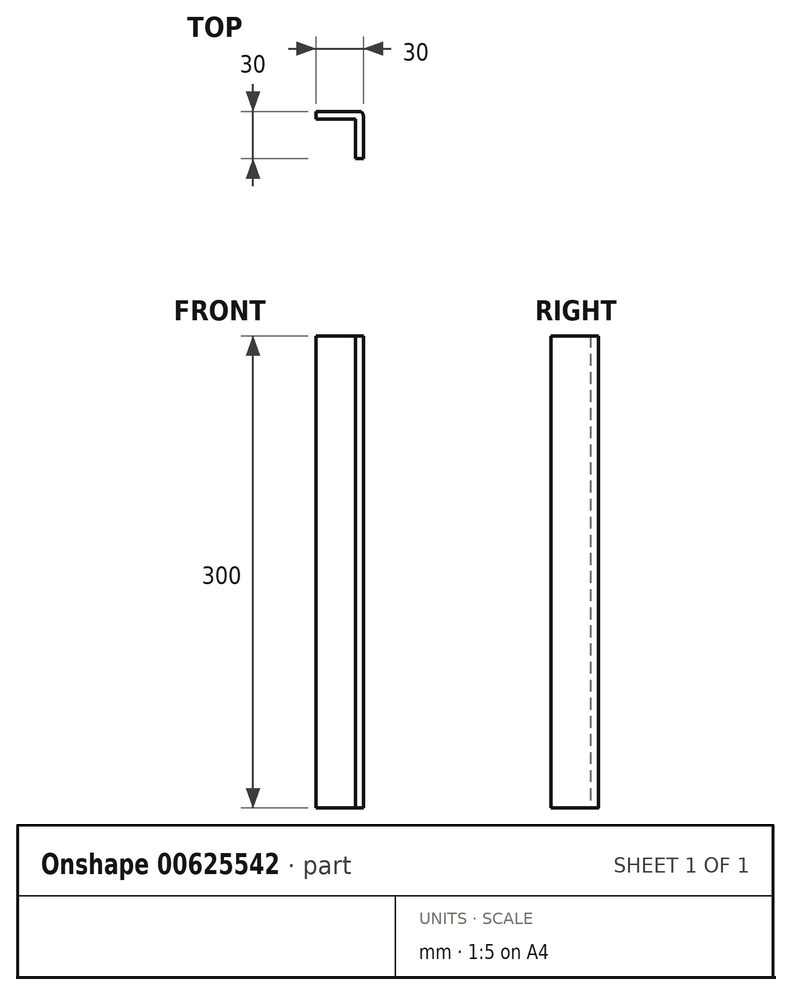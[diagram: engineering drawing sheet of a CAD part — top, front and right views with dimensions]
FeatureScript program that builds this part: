
annotation { "Feature Type Name" : "Feature", "Feature Type Description" : "" }
export const myFeature = defineFeature(function(context is Context, id is Id, definition is map)
    precondition{}
    {
        {
            var Q0;
            Q0=qCreatedBy(makeId("Top.planeOp"),FACE);
            var sketch = newSketch(context, id + "F0", { "sketchPlane" : qUnion([Q0])});
            skLineSegment(sketch, "E0.bottom", {"start": v(-15, 15) * mm, "end": v(12.5, 15) * mm});
            skLineSegment(sketch, "E0.top", {"start": v(10, -15) * mm, "end": v(15, -15) * mm});
            skLineSegment(sketch, "E0.left", {"start": v(-15, 15) * mm, "end": v(-15, 10) * mm});
            skLineSegment(sketch, "E0.right", {"start": v(15, 12.5) * mm, "end": v(15, -15) * mm});
            skPoint(sketch, "E0.middle", {"position": v(0, 0) * mm});
            skLineSegment(sketch, "E1", {"start": v(-15, 10) * mm, "end": v(10, 10) * mm});
            skLineSegment(sketch, "E2", {"start": v(10, 10) * mm, "end": v(10, -15) * mm});
            skPoint(sketch, "E3.visualSharp", {"position": v(10, 10) * mm});
            skLineSegment(sketch, "E3.filletArc", {"start": v(10, 10) * mm, "end": v(10, 10) * mm});
            skPoint(sketch, "E4.visualSharp", {"position": v(15, 15) * mm});
            skArc(sketch, "E4.filletArc", {"start": v(15, 12.5) * mm, "mid": v(14.27, 14.27) * mm, "end": v(12.5, 15) * mm});
            skPoint(sketch, "E5.orphan", {"position": v(-15, -15) * mm});
            skSolve(sketch);
        }
        {
            var Q0;
            Q0 = qSketchRegion(id + "F0", true);
            extrude(context, id + "F1", {"entities" : qUnion([Q0]), "depth" : 300 * mm, "offsetDistance" : 25 * mm});
        }
    });
